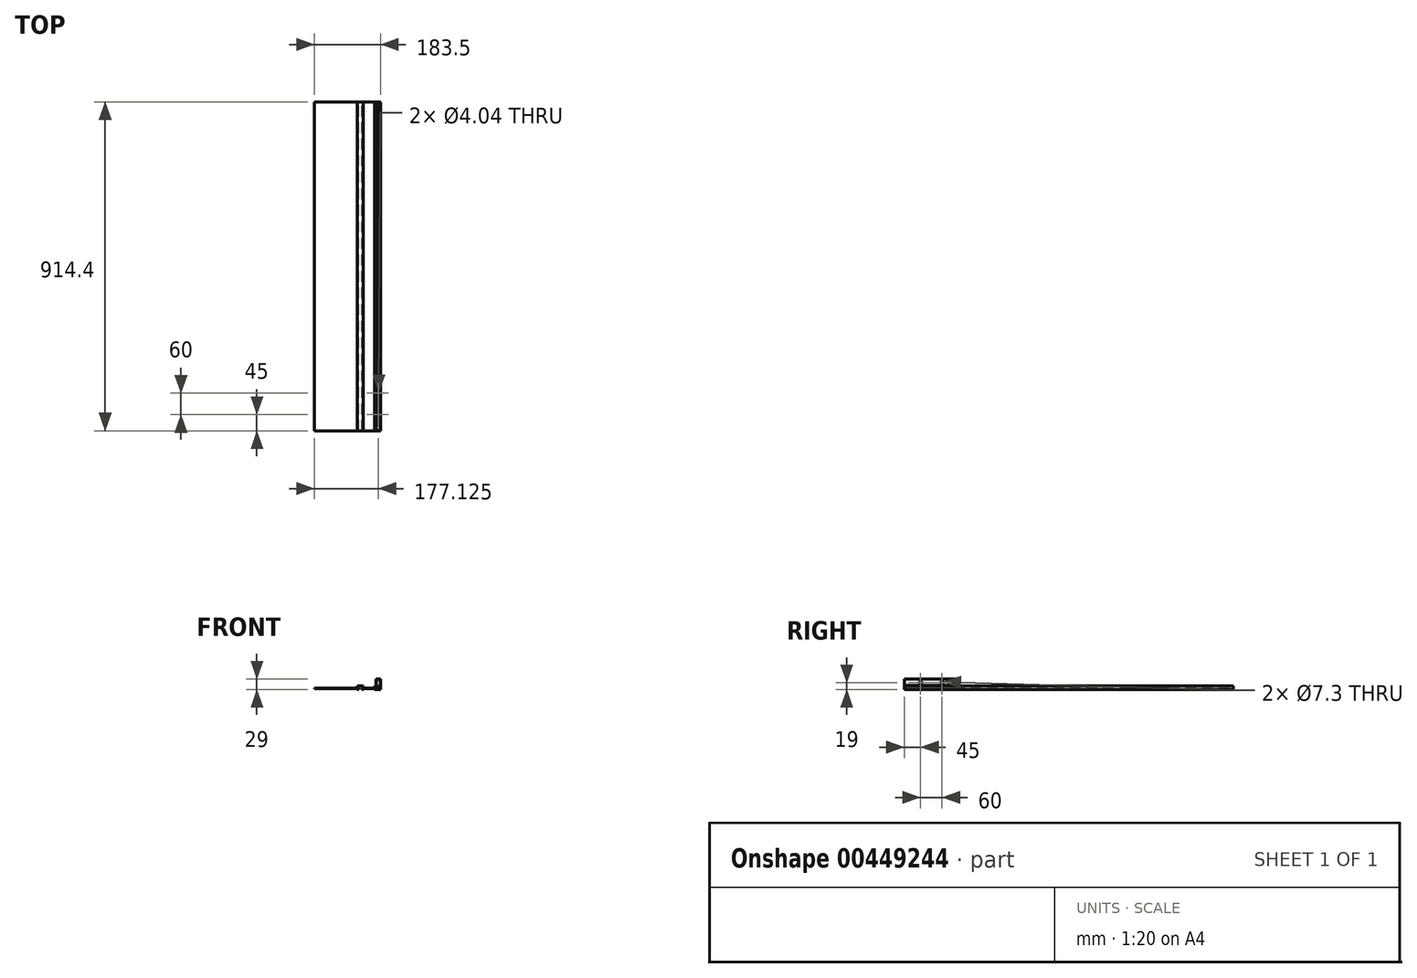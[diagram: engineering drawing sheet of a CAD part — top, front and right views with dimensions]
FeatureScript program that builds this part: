
annotation { "Feature Type Name" : "Feature", "Feature Type Description" : "" }
export const myFeature = defineFeature(function(context is Context, id is Id, definition is map)
    precondition{}
    {
        {
            var Q0;
            Q0=qCreatedBy(makeId("Front.planeOp"),FACE);
            var sketch = newSketch(context, id + "F0", { "sketchPlane" : qUnion([Q0])});
            skLineSegment(sketch, "E0", {"start": v(-16.5, 0) * mm, "end": v(-16.5, 0) * mm});
            skLineSegment(sketch, "E1", {"start": v(-16.5, 0) * mm, "end": v(-48.5, 0) * mm});
            skLineSegment(sketch, "E2", {"start": v(-48.5, 0) * mm, "end": v(-48.5, 0) * mm});
            skLineSegment(sketch, "E3", {"start": v(-46, 0) * mm, "end": v(-46, 0) * mm});
            skLineSegment(sketch, "E4", {"start": v(-183.5, 0) * mm, "end": v(-183.5, 2) * mm});
            skLineSegment(sketch, "E5", {"start": v(-183.5, 2) * mm, "end": v(-64.5, 2) * mm});
            skLineSegment(sketch, "E6", {"start": v(-64.5, 2) * mm, "end": v(-64.5, 8.5) * mm});
            skLineSegment(sketch, "E7", {"start": v(-64.5, 8.5) * mm, "end": v(-48.5, 8.5) * mm});
            skLineSegment(sketch, "E8", {"start": v(-48.5, 8.5) * mm, "end": v(-48.5, 2) * mm});
            skLineSegment(sketch, "E9", {"start": v(-48.5, 2) * mm, "end": v(-16.5, 2) * mm});
            skLineSegment(sketch, "E10", {"start": v(-16.5, 2) * mm, "end": v(-16.5, 8.5) * mm});
            skLineSegment(sketch, "E11", {"start": v(-16.5, 8.5) * mm, "end": v(-12.75, 8.5) * mm});
            skLineSegment(sketch, "E12", {"start": v(-12.75, 8.5) * mm, "end": v(-12.75, 6.5) * mm});
            skLineSegment(sketch, "E13", {"start": v(-12.75, 6.5) * mm, "end": v(-14.5, 6.5) * mm});
            skLineSegment(sketch, "E14", {"start": v(-14.5, 6.5) * mm, "end": v(-14.5, 0) * mm});
            skLineSegment(sketch, "E15", {"start": v(-14.5, 0) * mm, "end": v(-2, 0) * mm});
            skLineSegment(sketch, "E16", {"start": v(-2, 0) * mm, "end": v(-2, 6.5) * mm});
            skLineSegment(sketch, "E17", {"start": v(-2, 6.5) * mm, "end": v(-3.75, 6.5) * mm});
            skLineSegment(sketch, "E18", {"start": v(-3.75, 6.5) * mm, "end": v(-3.75, 8.5) * mm});
            skLineSegment(sketch, "E19", {"start": v(-3.75, 8.5) * mm, "end": v(0, 8.5) * mm});
            skLineSegment(sketch, "E20", {"start": v(0, 8.5) * mm, "end": v(0, 0) * mm});
            skLineSegment(sketch, "E21", {"start": v(0, 0) * mm, "end": v(0, -2) * mm});
            skLineSegment(sketch, "E22", {"start": v(0, -2) * mm, "end": v(-16.5, -2) * mm});
            skLineSegment(sketch, "E23", {"start": v(-16.5, -2) * mm, "end": v(-16.5, 0) * mm});
            skLineSegment(sketch, "E24", {"start": v(-183.5, 0) * mm, "end": v(-64.5, 0) * mm});
            skLineSegment(sketch, "E25", {"start": v(-64.5, 0) * mm, "end": v(-64.5, -2) * mm});
            skLineSegment(sketch, "E26", {"start": v(-64.5, -2) * mm, "end": v(-60.75, -2) * mm});
            skLineSegment(sketch, "E27", {"start": v(-60.75, -2) * mm, "end": v(-60.75, 0) * mm});
            skLineSegment(sketch, "E28", {"start": v(-60.75, 0) * mm, "end": v(-62.5, 0) * mm});
            skLineSegment(sketch, "E29", {"start": v(-62.5, 0) * mm, "end": v(-62.5, 6.5) * mm});
            skLineSegment(sketch, "E30", {"start": v(-62.5, 6.5) * mm, "end": v(-50.5, 6.5) * mm});
            skLineSegment(sketch, "E31", {"start": v(-50.5, 6.5) * mm, "end": v(-50.5, 0) * mm});
            skLineSegment(sketch, "E32", {"start": v(-50.5, 0) * mm, "end": v(-52.25, 0) * mm});
            skLineSegment(sketch, "E33", {"start": v(-52.25, 0) * mm, "end": v(-52.25, -2) * mm});
            skLineSegment(sketch, "E34", {"start": v(-52.25, -2) * mm, "end": v(-48.5, -2) * mm});
            skLineSegment(sketch, "E35", {"start": v(-48.5, -2) * mm, "end": v(-48.5, 0) * mm});
            skSolve(sketch);
        }
        {
            var Q0;
            Q0 = qSketchRegion(id + "F0", true);
            extrude(context, id + "F1", {"entities" : qUnion([Q0]), "depth" : 914.4 * mm});
        }
        {
            var Q0;
            Q0=makeQuery(id+"F1.opExtrude","CAP_FACE",FACE,{"disambiguationData":[OSD([sQuery(id+"F0.wireOp",EDGE,"E1"),sQuery(id+"F0.wireOp",EDGE,"E4"),sQuery(id+"F0.wireOp",EDGE,"E5"),sQuery(id+"F0.wireOp",EDGE,"E6"),sQuery(id+"F0.wireOp",EDGE,"E7"),sQuery(id+"F0.wireOp",EDGE,"E8"),sQuery(id+"F0.wireOp",EDGE,"E9"),sQuery(id+"F0.wireOp",EDGE,"E10"),sQuery(id+"F0.wireOp",EDGE,"E11"),sQuery(id+"F0.wireOp",EDGE,"E12"),sQuery(id+"F0.wireOp",EDGE,"E13"),sQuery(id+"F0.wireOp",EDGE,"E14"),sQuery(id+"F0.wireOp",EDGE,"E15"),sQuery(id+"F0.wireOp",EDGE,"E16"),sQuery(id+"F0.wireOp",EDGE,"E17"),sQuery(id+"F0.wireOp",EDGE,"E18"),sQuery(id+"F0.wireOp",EDGE,"E19"),sQuery(id+"F0.wireOp",EDGE,"E20"),sQuery(id+"F0.wireOp",EDGE,"E21"),sQuery(id+"F0.wireOp",EDGE,"E22"),sQuery(id+"F0.wireOp",EDGE,"E23"),sQuery(id+"F0.wireOp",EDGE,"E24"),sQuery(id+"F0.wireOp",EDGE,"E25"),sQuery(id+"F0.wireOp",EDGE,"E26"),sQuery(id+"F0.wireOp",EDGE,"E27"),sQuery(id+"F0.wireOp",EDGE,"E28"),sQuery(id+"F0.wireOp",EDGE,"E29"),sQuery(id+"F0.wireOp",EDGE,"E30"),sQuery(id+"F0.wireOp",EDGE,"E31"),sQuery(id+"F0.wireOp",EDGE,"E32"),sQuery(id+"F0.wireOp",EDGE,"E33"),sQuery(id+"F0.wireOp",EDGE,"E34"),sQuery(id+"F0.wireOp",EDGE,"E35")])],"isStart":false});
            var sketch = newSketch(context, id + "F2", { "sketchPlane" : qUnion([Q0])});
            skLineSegment(sketch, "E36.0", {"start": v(-3.75, 6.5) * mm, "end": v(-3.75, 8.5) * mm});
            skLineSegment(sketch, "E36.1", {"start": v(-2, 6.5) * mm, "end": v(-3.75, 6.5) * mm});
            skLineSegment(sketch, "E36.2", {"start": v(-2, 0) * mm, "end": v(-2, 6.5) * mm});
            skLineSegment(sketch, "E36.3", {"start": v(-12.75, 8.5) * mm, "end": v(-12.75, 6.5) * mm});
            skLineSegment(sketch, "E36.4", {"start": v(-12.75, 6.5) * mm, "end": v(-14.5, 6.5) * mm});
            skLineSegment(sketch, "E36.5", {"start": v(-14.5, 6.5) * mm, "end": v(-14.5, 0) * mm});
            skLineSegment(sketch, "E36.6", {"start": v(-14.5, 0) * mm, "end": v(-2, 0) * mm});
            skLineSegment(sketch, "E37", {"start": v(-12.75, 8.5) * mm, "end": v(-12.75, 27) * mm});
            skLineSegment(sketch, "E38", {"start": v(-12.75, 27) * mm, "end": v(-3.75, 27) * mm});
            skLineSegment(sketch, "E39", {"start": v(-3.75, 8.5) * mm, "end": v(-3.75, 27) * mm});
            skPoint(sketch, "E40.orphan", {"position": v(-3.75, 27) * mm});
            skSolve(sketch);
        }
        {
            var Q0;
            Q0 = qSketchRegion(id + "F2", true);
            extrude(context, id + "F3", {"entities" : qUnion([Q0]), "oppositeDirection" : true, "depth" : 150 * mm});
        }
        {
            var Q0;
            Q0=makeQuery(id+"F3.opExtrude","SWEPT_FACE",FACE,{"disambiguationData":[OSD([sQuery(id+"F2.wireOp",EDGE,"E36.0"),sQuery(id+"F2.wireOp",EDGE,"E39")])]});
            var sketch = newSketch(context, id + "F4", { "sketchPlane" : qUnion([Q0])});
            skLineSegment(sketch, "E41.bottom", {"start": v(-914.4, 27) * mm, "end": v(-764.4, 27) * mm});
            skLineSegment(sketch, "E41.top", {"start": v(-914.4, 8.51) * mm, "end": v(-764.4, 8.51) * mm});
            skLineSegment(sketch, "E41.left", {"start": v(-914.4, 27) * mm, "end": v(-914.4, 8.51) * mm});
            skLineSegment(sketch, "E41.right", {"start": v(-764.4, 27) * mm, "end": v(-764.4, 8.51) * mm});
            skSolve(sketch);
        }
        {
            var Q0;
            Q0 = qSketchRegion(id + "F4", true);
            var Q1;
            Q1=makeQuery(id+"F1.opExtrude","SWEPT_FACE",FACE,{"disambiguationData":[OSD([sQuery(id+"F0.wireOp",EDGE,"E20"),sQuery(id+"F0.wireOp",EDGE,"E21")])]});
            extrude(context, id + "F5", {"entities" : qUnion([Q0]), "operationType" : NewBodyOperationType.ADD, "endBound" : BoundingType.UP_TO_SURFACE, "endBoundEntityFace" : qUnion([Q1]), "depth" : 25 * mm});
        }
        {
            var Q0;
            Q0=makeQuery(id+"F5.opExtrude","CAP_FACE",FACE,{"disambiguationData":[OSD([sQuery(id+"F4.wireOp",EDGE,"E41.bottom"),sQuery(id+"F4.wireOp",EDGE,"E41.top"),sQuery(id+"F4.wireOp",EDGE,"E41.left"),sQuery(id+"F4.wireOp",EDGE,"E41.right")])],"isStart":false});
            var sketch = newSketch(context, id + "F6", { "sketchPlane" : qUnion([Q0])});
            skLineSegment(sketch, "E42", {"start": v(-839.4, 27) * mm, "end": v(-839.4, 6.5) * mm, "construction": true});
            skCircle(sketch, "E43", {"center": v(-869.4, 17) * mm, "radius": 3.65 * mm});
            skCircle(sketch, "E44.MirrorC", {"center": v(-809.4, 17) * mm, "radius": 3.65 * mm});
            skSolve(sketch);
        }
        {
            var Q0;
            Q0 = qSketchRegion(id + "F6", true);
            extrude(context, id + "F7", {"entities" : qUnion([Q0]), "operationType" : NewBodyOperationType.REMOVE, "endBound" : BoundingType.THROUGH_ALL, "oppositeDirection" : true, "depth" : 25 * mm});
        }
        {
            var Q0;
            Q0=makeQuery(id+"F5.boolean.opBoolean","MERGE",FACE,{"derivedFrom":[makeQuery(id+"F3.opExtrude","SWEPT_FACE",FACE,{"disambiguationData":[OSD([sQuery(id+"F2.wireOp",EDGE,"E38")])]}),makeQuery(id+"F5.opExtrude","SWEPT_FACE",FACE,{"disambiguationData":[OSD([sQuery(id+"F4.wireOp",EDGE,"E41.bottom")])]})]});
            var sketch = newSketch(context, id + "F8", { "sketchPlane" : qUnion([Q0])});
            skLineSegment(sketch, "E45", {"start": v(-12.75, -839.4) * mm, "end": v(0, -839.4) * mm, "construction": true});
            skLineSegment(sketch, "E46", {"start": v(-6.37, -914.4) * mm, "end": v(-6.37, -764.4) * mm, "construction": true});
            skCircle(sketch, "E47", {"center": v(-6.37, -869.4) * mm, "radius": 2.02 * mm});
            skCircle(sketch, "E48.MirrorC", {"center": v(-6.37, -809.4) * mm, "radius": 2.02 * mm});
            skSolve(sketch);
        }
        {
            var Q0;
            Q0 = qSketchRegion(id + "F8", true);
            extrude(context, id + "F9", {"entities" : qUnion([Q0]), "operationType" : NewBodyOperationType.REMOVE, "endBound" : BoundingType.UP_TO_NEXT, "oppositeDirection" : true, "depth" : 25 * mm});
        }
        {
            var Q0;
            Q0=makeQuery(id+"F5.opExtrude","CAP_EDGE",EDGE,{"disambiguationData":[OSD([sQuery(id+"F4.wireOp",EDGE,"E41.bottom")])],"isStart":false});
            var Q1;
            Q1=makeQuery(id+"F5.opExtrude","CAP_EDGE",EDGE,{"disambiguationData":[OSD([sQuery(id+"F4.wireOp",EDGE,"E41.top")])],"isStart":false});
            var Q2;
            Q2=makeQuery(id+"F3.opExtrude","SWEPT_EDGE",EDGE,{"disambiguationData":[OSD([sQuery(id+"F2.wireOp",EDGE,"E36.1"),sQuery(id+"F2.wireOp",EDGE,"E36.2")])]});
            var Q3;
            Q3=makeQuery(id+"F3.opExtrude","SWEPT_EDGE",EDGE,{"disambiguationData":[OSD([sQuery(id+"F2.wireOp",EDGE,"E36.2"),sQuery(id+"F2.wireOp",EDGE,"E36.6")])]});
            var Q4;
            Q4=makeQuery(id+"F3.opExtrude","SWEPT_EDGE",EDGE,{"disambiguationData":[OSD([sQuery(id+"F2.wireOp",EDGE,"E36.5"),sQuery(id+"F2.wireOp",EDGE,"E36.6")])]});
            var Q5;
            Q5=makeQuery(id+"F3.opExtrude","SWEPT_EDGE",EDGE,{"disambiguationData":[OSD([sQuery(id+"F2.wireOp",EDGE,"E36.4"),sQuery(id+"F2.wireOp",EDGE,"E36.5")])]});
            var Q6;
            Q6=makeQuery(id+"F3.opExtrude","SWEPT_EDGE",EDGE,{"disambiguationData":[OSD([sQuery(id+"F2.wireOp",EDGE,"E37"),sQuery(id+"F2.wireOp",EDGE,"E38")])]});
            var Q7;
            Q7=makeQuery(id+"F5.opExtrude","CAP_EDGE",EDGE,{"disambiguationData":[OSD([sQuery(id+"F4.wireOp",EDGE,"E41.left")])],"isStart":false});
            var Q8;
            Q8=makeQuery(id+"F5.boolean.opBoolean","MERGE",EDGE,{"derivedFrom":[makeQuery(id+"F3.opExtrude","CAP_EDGE",EDGE,{"disambiguationData":[OSD([sQuery(id+"F2.wireOp",EDGE,"E38")])],"isStart":true}),makeQuery(id+"F5.opExtrude","SWEPT_EDGE",EDGE,{"disambiguationData":[OSD([sQuery(id+"F4.wireOp",EDGE,"E41.bottom"),sQuery(id+"F4.wireOp",EDGE,"E41.left")])]})]});
            var Q9;
            Q9=makeQuery(id+"F3.opExtrude","CAP_EDGE",EDGE,{"disambiguationData":[OSD([sQuery(id+"F2.wireOp",EDGE,"E36.3"),sQuery(id+"F2.wireOp",EDGE,"E37")])],"isStart":true});
            var Q10;
            Q10=makeQuery(id+"F3.opExtrude","CAP_EDGE",EDGE,{"disambiguationData":[OSD([sQuery(id+"F2.wireOp",EDGE,"E36.6")])],"isStart":true});
            var Q11;
            Q11=makeQuery(id+"F5.boolean.opBoolean","MERGE",EDGE,{"derivedFrom":[makeQuery(id+"F3.opExtrude","CAP_EDGE",EDGE,{"disambiguationData":[OSD([sQuery(id+"F2.wireOp",EDGE,"E38")])],"isStart":false}),makeQuery(id+"F5.opExtrude","SWEPT_EDGE",EDGE,{"disambiguationData":[OSD([sQuery(id+"F4.wireOp",EDGE,"E41.bottom"),sQuery(id+"F4.wireOp",EDGE,"E41.right")])]})]});
            var Q12;
            Q12=makeQuery(id+"F5.opExtrude","CAP_EDGE",EDGE,{"disambiguationData":[OSD([sQuery(id+"F4.wireOp",EDGE,"E41.right")])],"isStart":false});
            var Q13;
            Q13=makeQuery(id+"F3.opExtrude","CAP_EDGE",EDGE,{"disambiguationData":[OSD([sQuery(id+"F2.wireOp",EDGE,"E36.3"),sQuery(id+"F2.wireOp",EDGE,"E37")])],"isStart":false});
            var Q14;
            Q14=makeQuery(id+"F3.opExtrude","CAP_EDGE",EDGE,{"disambiguationData":[OSD([sQuery(id+"F2.wireOp",EDGE,"E36.6")])],"isStart":false});
            var Q15;
            Q15=makeQuery(id+"F3.opExtrude","CAP_EDGE",EDGE,{"disambiguationData":[OSD([sQuery(id+"F2.wireOp",EDGE,"E36.0"),sQuery(id+"F2.wireOp",EDGE,"E39")])],"isStart":false});
            var Q16;
            Q16=makeQuery(id+"F3.opExtrude","CAP_EDGE",EDGE,{"disambiguationData":[OSD([sQuery(id+"F2.wireOp",EDGE,"E36.1")])],"isStart":false});
            var Q17;
            Q17=makeQuery(id+"F3.opExtrude","CAP_EDGE",EDGE,{"disambiguationData":[OSD([sQuery(id+"F2.wireOp",EDGE,"E36.4")])],"isStart":false});
            var Q18;
            Q18=makeQuery(id+"F3.opExtrude","CAP_EDGE",EDGE,{"disambiguationData":[OSD([sQuery(id+"F2.wireOp",EDGE,"E36.4")])],"isStart":true});
            var Q19;
            Q19=makeQuery(id+"F5.opExtrude","SWEPT_EDGE",EDGE,{"disambiguationData":[OSD([sQuery(id+"F2.wireOp",EDGE,"E36.0"),sQuery(id+"F2.wireOp",EDGE,"E39"),sQuery(id+"F4.wireOp",EDGE,"E41.top"),sQuery(id+"F4.wireOp",EDGE,"E41.left")])]});
            var Q20;
            Q20=makeQuery(id+"F3.opExtrude","CAP_EDGE",EDGE,{"disambiguationData":[OSD([sQuery(id+"F2.wireOp",EDGE,"E36.1")])],"isStart":true});
            chamfer(context, id + "F10", {"entities" : qUnion([Q0, Q1, Q2, Q3, Q4, Q5, Q6, Q7, Q8, Q9, Q10, Q11, Q12, Q13, Q14, Q15, Q16, Q17, Q18, Q19, Q20]), "width" : .5 * mm, "tangentPropagation" : true});
        }
        {
            var Q0;
            Q0=makeQuery(id+"F7.boolean.opBoolean","INTERSECT",EDGE,{"derivedFrom":[makeQuery(id+"F3.opExtrude","SWEPT_FACE",FACE,{"disambiguationData":[OSD([sQuery(id+"F2.wireOp",EDGE,"E36.3"),sQuery(id+"F2.wireOp",EDGE,"E37")])]}),makeQuery(id+"F7.opExtrude","SWEPT_FACE",FACE,{"disambiguationData":[OSD([sQuery(id+"F6.wireOp",EDGE,"E44.MirrorC")])]})]});
            var Q1;
            Q1=makeQuery(id+"F7.boolean.opBoolean","INTERSECT",EDGE,{"derivedFrom":[makeQuery(id+"F3.opExtrude","SWEPT_FACE",FACE,{"disambiguationData":[OSD([sQuery(id+"F2.wireOp",EDGE,"E36.3"),sQuery(id+"F2.wireOp",EDGE,"E37")])]}),makeQuery(id+"F7.opExtrude","SWEPT_FACE",FACE,{"disambiguationData":[OSD([sQuery(id+"F6.wireOp",EDGE,"E43")])]})]});
            var Q2;
            Q2=makeQuery(id+"F9.boolean.opBoolean","COPY",EDGE,{"derivedFrom":makeQuery(id+"F9.opExtrude","CAP_EDGE",EDGE,{"disambiguationData":[OSD([sQuery(id+"F8.wireOp",EDGE,"E48.MirrorC")])],"isStart":true})});
            var Q3;
            Q3=makeQuery(id+"F9.boolean.opBoolean","COPY",EDGE,{"derivedFrom":makeQuery(id+"F9.opExtrude","CAP_EDGE",EDGE,{"disambiguationData":[OSD([sQuery(id+"F8.wireOp",EDGE,"E47")])],"isStart":true})});
            var Q4;
            Q4=makeQuery(id+"F7.boolean.opBoolean","COPY",EDGE,{"derivedFrom":makeQuery(id+"F7.opExtrude","CAP_EDGE",EDGE,{"disambiguationData":[OSD([sQuery(id+"F6.wireOp",EDGE,"E43")])],"isStart":true})});
            var Q5;
            Q5=makeQuery(id+"F7.boolean.opBoolean","COPY",EDGE,{"derivedFrom":makeQuery(id+"F7.opExtrude","CAP_EDGE",EDGE,{"disambiguationData":[OSD([sQuery(id+"F6.wireOp",EDGE,"E44.MirrorC")])],"isStart":true})});
            fillet(context, id + "F11", {"entities" : qUnion([Q0, Q1, Q2, Q3, Q4, Q5]), "radius" : 0.5 * mm, "tangentPropagation" : true, "allowEdgeOverflow" : false});
        }
    });
